# Revit family: ACO AUS Gully 157 Telescopic - Square Top - Vertical Outlet with Mechanical Flange - 200x200 3
name_source: partatom
category: Plumbing Fixtures
revit_build: Autodesk Revit 2014 (Build: 20130308_1515(x64)
units: mm (PartAtom-declared; Revit-internal decimal feet)

## types (4) — shared parameters
408057 - Telescopic Vertical Gully & 408205 - Friction Ring = Yes
Fax = +61 (2) 4747 4029
Grating 200 x 200mm = Yes
Grating Depth = 25 mm  [stored 0.082021 ft]
Gully Colour = passivated stainless steel surface ( matt grey)
Gully Recyclable = Fully Recyclable
Gully Recycled Material Content = 20 - 30 %
Gully Top = Yes
Gully Top Size (mm) = To suit 200x200 grates
Load Class = A15 - C250 (EN 1253) and D210 (AS 3996)
Manufacturer = ACO Polycrete
Outlet Diameter (mm) = 110
Price = POA - contact ACO
Product Range = ACO Gully 157
Product Type = Point Drainage
Seepage Water Removal Pipe End = -8.5 mm
Square Size = 200 mm  [stored 0.656168 ft]
Telephone = +61 (2) 4747 4000
Waste Connection = No
Water Mark 1 = This file is the property of ACO Passavant
Water Mark 2 = This file is water marked and users are prohibited to reproduce, adapt, distribute this information
Water Marked With = BIM Manager Premium Suite
Website = www.acoaus.com.au

## per-type parameters (varying)
- 142188 - Adjustable Height without FAT SS 304: Flow Rate (l/s)=12.6; Foul Air Trap &  Foul Air Trap Support Ring=No; Grating Product Code 142009=Load Class L15 (EN 1253) - 5 Star Grating - Slip Resistant  - Stainless steel grade 304 - 168 x 168 x 25mm - 1.1kg; Grating Product Code 408023=Load Class L15 (EN 1253) - Arla Grating - Slip Resistant - Stainless steel grade 304 - 168 x 168 x 25mm - 0.7kg; Grating Product Code 408043=Load Class D210 (EN 1253) - Ladder Grating - Plain  - Stainless steel grade 304 - 168 x 168 x 25mm - 2.2kg; Grating Product Code 408090=Load Class L15 (EN 1253) - Mesh Grating - Slip Resistant - Stainless steel grade 304 - 168 x 168 x 25mm - 0.8kg; Grating Product Code 408091=Load Class L15 (EN 1253) - Mesh Grating - Plain - Stainless steel grade 304 - 168 x 168 x 25mm - 0.8kg; Grating Product Code 408093=Load Class M125 (EN 1253) - Ladder Grating - Slip Resistant  - Stainless steel grade 304 - 168 x 168 x 25mm - 1.9kg; Grating Product Code 416912=Load Class R50 (EN 1253) - Ladder Grating - Slip Resistant  - Stainless steel grade 304 - 168 x 168 x 25mm - 1.6kg; Grating Product Code 416942=Load Class M125 (EN 1253) - Cast Grating - Slip Resistant  - Stainless steel grade 304 - 168 x 168 x 25mm - 2.1kg; Gully Material=Stainless steel grade 304; Gully Product Code=142188; Gully Product Description=ACO Gully 157 adjustable height gully with integrated clamping flange - DN100 vertical outlet with square top section without FAT - grade 304; Gully Weight (Kg)=4; Material=Stainless Steel AISI 304; Product Code 408203=0.3 litre removable strainer - Stainless steel grade 304 - 0.3kg; Product Code 408206=Waterproof bonding flange - Stainless steel grade 304 - 1.9kg; Product Code 413026=1.0 litre removable strainer -Stainless steel grade 304 -  0.6kg
- 142189 - Adjustable Height without FAT SS 316: Flow Rate (l/s)=12.6; Foul Air Trap &  Foul Air Trap Support Ring=No; Grating Product Code 408123=Load Class L15 (EN 1253) - Arla Grating - Slip Resistant - Stainless steel grade 316 - 168 x 168 x 25mm - 0.7kg; Grating Product Code 408143=Load Class D210 (EN 1253) - Ladder Grating - Plain  -Stainless steel grade 316 - 168 x 168 x 25mm - 2.2kg; Grating Product Code 408190=Load Class L15 (EN 1253) - Mesh Grating - Slip Resistant - Stainless steel grade 316 - 168 x 168 x 25mm - 0.8kg; Grating Product Code 408191=Load Class L15 (EN 1253) - Mesh Grating - Plain - Stainless steel grade 316 - 168 x 168 x 25mm - 0.8kg; Grating Product Code 408193=Load Class M125 (EN 1253) - Ladder Grating - Slip Resistant  - Stainless steel grade 316 - 168 x 168 x 25mm - 1.9kg; Grating Product Code 416913=Load Class R50 (EN 1253) - Ladder Grating - Slip Resistant  - Stainless steel grade 316 - 168 x 168 x 25mm - 1.6kg; Gully Material=Stainless steel grade 316; Gully Product Code=142189; Gully Product Description=ACO Gully 157 adjustable height gully with integrated clamping flange - DN100 vertical outlet with square top section without FAT - grade 316; Gully Weight (Kg)=4; Material=Stainless Steel AISI 316; Product Code 142001=Fixed  strainer to suit a 110mm outlet -  Stainless steel grade 316 - 0.1kg; Product Code 142003=Retention chain connecting fixed (secondary) strainer to removable (primary) strainer -Stainless steel grade 316 - 0.1kg; Product Code 142005=Retention chain connecting removable (primary) strainer to grate - Stainless steel grade 316 - 0.1kg; Product Code 408213=0.3 litre removable strainer - Stainless steel grade 316 - 0.3kg; Product Code 408216=Waterproof bonding flange - Stainless steel grade 316 - 1.9kg; Product Code 413027=1.0 litre removable strainer - Stainless steel grade 316 - 0.6kg
- 142190 - Adjustable Height with FAT SS 304: Flow Rate (l/s)=3.5-4; Foul Air Trap &  Foul Air Trap Support Ring=Yes; Foul Air Trap Seal Colour=Black; Foul Air Trap Seal Material=NBR; Foul Air Trap Seal Recyclable=Fully Recyclable; Foul Air Trap Seal Recycled Material Content=0%; Grating Product Code 142009=Load Class L15 (EN 1253) - 5 Star Grating - Slip Resistant  - Stainless steel grade 304 - 168 x 168 x 25mm - 1.1kg; Grating Product Code 408023=Load Class L15 (EN 1253) - Arla Grating - Slip Resistant - Stainless steel grade 304 - 168 x 168 x 25mm - 0.7kg; Grating Product Code 408043=Load Class D210 (EN 1253) - Ladder Grating - Plain  - Stainless steel grade 304 - 168 x 168 x 25mm - 2.2kg; Grating Product Code 408090=Load Class L15 (EN 1253) - Mesh Grating - Slip Resistant - Stainless steel grade 304 - 168 x 168 x 25mm - 0.8kg; Grating Product Code 408091=Load Class L15 (EN 1253) - Mesh Grating - Plain - Stainless steel grade 304 - 168 x 168 x 25mm - 0.8kg; Grating Product Code 408093=Load Class M125 (EN 1253) - Ladder Grating - Slip Resistant  - Stainless steel grade 304 - 168 x 168 x 25mm - 1.9kg; Grating Product Code 416912=Load Class R50 (EN 1253) - Ladder Grating - Slip Resistant  - Stainless steel grade 304 - 168 x 168 x 25mm - 1.6kg; Grating Product Code 416942=Load Class M125 (EN 1253) - Cast Grating - Slip Resistant  - Stainless steel grade 304 - 168 x 168 x 25mm - 2.1kg; Gully Material=Stainless steel grade 304; Gully Product Code=142190; Gully Product Description=ACO Gully 157 adjustable height gully with integrated clamping flange - DN100 vertical outlet with square top section with FAT - grade 304; Gully Weight (Kg)=4.7; Material=Stainless Steel AISI 304; Product Code 408203=0.3 litre removable strainer - Stainless steel grade 304 - 0.3kg; Product Code 408206=Waterproof bonding flange - Stainless steel grade 304 - 1.9kg; Product Code 413026=1.0 litre removable strainer -Stainless steel grade 304 -  0.6kg
- 142191 - Adjustable Height with FAT SS 316: Flow Rate (l/s)=3.5-4; Foul Air Trap &  Foul Air Trap Support Ring=Yes; Foul Air Trap Seal Colour=Black; Foul Air Trap Seal Material=NBR; Foul Air Trap Seal Recyclable=Fully Recyclable; Foul Air Trap Seal Recycled Material Content=0%; Grating Product Code 408123=Load Class L15 (EN 1253) - Arla Grating - Slip Resistant - Stainless steel grade 316 - 168 x 168 x 25mm - 0.7kg; Grating Product Code 408143=Load Class D210 (EN 1253) - Ladder Grating - Plain  -Stainless steel grade 316 - 168 x 168 x 25mm - 2.2kg; Grating Product Code 408190=Load Class L15 (EN 1253) - Mesh Grating - Slip Resistant - Stainless steel grade 316 - 168 x 168 x 25mm - 0.8kg; Grating Product Code 408191=Load Class L15 (EN 1253) - Mesh Grating - Plain - Stainless steel grade 316 - 168 x 168 x 25mm - 0.8kg; Grating Product Code 408193=Load Class M125 (EN 1253) - Ladder Grating - Slip Resistant  - Stainless steel grade 316 - 168 x 168 x 25mm - 1.9kg; Grating Product Code 416913=Load Class R50 (EN 1253) - Ladder Grating - Slip Resistant  - Stainless steel grade 316 - 168 x 168 x 25mm - 1.6kg; Gully Material=Stainless steel grade 316; Gully Product Code=142191; Gully Product Description=ACO Gully 157 adjustable height gully with integrated clamping flange - DN100 vertical outlet with square top section with FAT - grade 316; Gully Weight (Kg)=4.7; Material=Stainless Steel AISI 316; Product Code 142001=Fixed  strainer to suit a 110mm outlet -  Stainless steel grade 316 - 0.1kg; Product Code 142002=Retention chain connecting fixed (secondary) strainer to FAT - Stainless steel grade 316 - 0.1kg; Product Code 142003=Retention chain connecting fixed (secondary) strainer to removable (primary) strainer -Stainless steel grade 316 - 0.1kg; Product Code 142004=Retention chain connecting to FAT to removable (primary) strainer - Stainless steel grade 316 - 0.1kg; Product Code 142005=Retention chain connecting removable (primary) strainer to grate - Stainless steel grade 316 - 0.1kg; Product Code 142006=Retention chain connecting removable FAT to grate - Stainless steel grade 316 - 0.1kg; Product Code 408213=0.3 litre removable strainer - Stainless steel grade 316 - 0.3kg; Product Code 408216=Waterproof bonding flange - Stainless steel grade 316 - 1.9kg; Product Code 413027=1.0 litre removable strainer - Stainless steel grade 316 - 0.6kg

note: [stored X ft] marks values corroborated as IEEE doubles in the binary element streams (Revit-internal decimal feet)

## geometry (parser evidence)
native form markers: Blend x6, Sweep x4
no freeform markers — native parametric forms only
